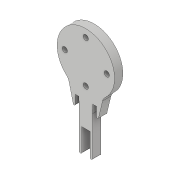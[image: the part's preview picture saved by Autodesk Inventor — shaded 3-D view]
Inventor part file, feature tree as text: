
AUTODESK INVENTOR PART (.ipt)
format: ipt  version: 2017 (Build 210142000, 142)  size: 231,936 bytes
history: native  units: in
note: dims shown in document units (in); Inventor stores cm internally (conversion verified against a paired STEP export)
features: sketch x7, extrude x4, projected_geometry x4, fillet x2, chamfer x2, other x2, plane x2, sheet_metal_op x1, hole x1
ambient origin geometry x8: Origin, YZ Plane, XZ Plane, XY Plane, X Axis, Y Axis, Z Axis, Center Point
bodies: Solid1 (feature_tree)
feature tree (25):
  sheet_metal_op  "Face1"
  extrude  "Extrusion1"  Depth=0.3937in
  sketch  "Sketch3"  dims[d10=0.25in d11=0.25in]
  fillet  "Fillet4"  Radius=0.5512in
  extrude  "Extrusion2"  Depth=0.0623in
  extrude  "Extrusion3"  Depth=0.25in
  extrude  "Extrusion4"  Depth=0.125in
  fillet  "Fillet5"  Radius=1.0in
  chamfer  "Chamfer3"  Distance=0.125in
  chamfer  "Chamfer4"  Distance=0.2004in
  hole  "Hole1"  [1 undecoded]
  other  "Work Axis1"
  sketch  "Sketch1"  dims[d2=0.1969in d3=0.3937in d4=0.5512in]
  other  "Plate1"
  sketch  "Sketch2"  dims[d8=0.0623in d9=0.0623in]
  projected_geometry  "Projected Loop1"
  sketch  "Sketch4"  dims[d12=0.125in d14=0.125in d15=1.0in d16=0.0in]
  projected_geometry  "Projected Loop2"
  sketch  "Sketch5"  dims[d18=0.0573in]
  projected_geometry  "Projected Loop3"
  sketch  "Sketch6"  dims[d19=0.0573in]
  sketch  "Sketch7"  dims[d28=0.2362in d29=0.125in d30=0.2004in d31=0.1in d32=0.1in d33=0.0in d34=0.0179in d35=0.315in d36=0.0573in d37=0.015in d38=1.0in d39=0.0in d40=0.1969in d42=1.0in d43=0.0in d44=0.1752in d45=0.862in d46=0.5in d47=1.0in d48=0.0in d49=0.125in d50=0.005in d51=0.125in d52=0.0137in d53=0.125in d54=0.005in d55=0.0137in d56=0.6299in d57=0.0787in d58=0.75in d59=0.375in d60=0.25in d61=0.5635in d62=0.125in d63=0.8108in]
  projected_geometry  "Projected Loop4"
  plane  "Work Plane1"
  plane  "Work Plane2"
note: 1 required parameter value undecoded (feature->parameter linkage not recoverable at this tier; creation-order binding heuristic only, values carry confidence <= 0.55)
